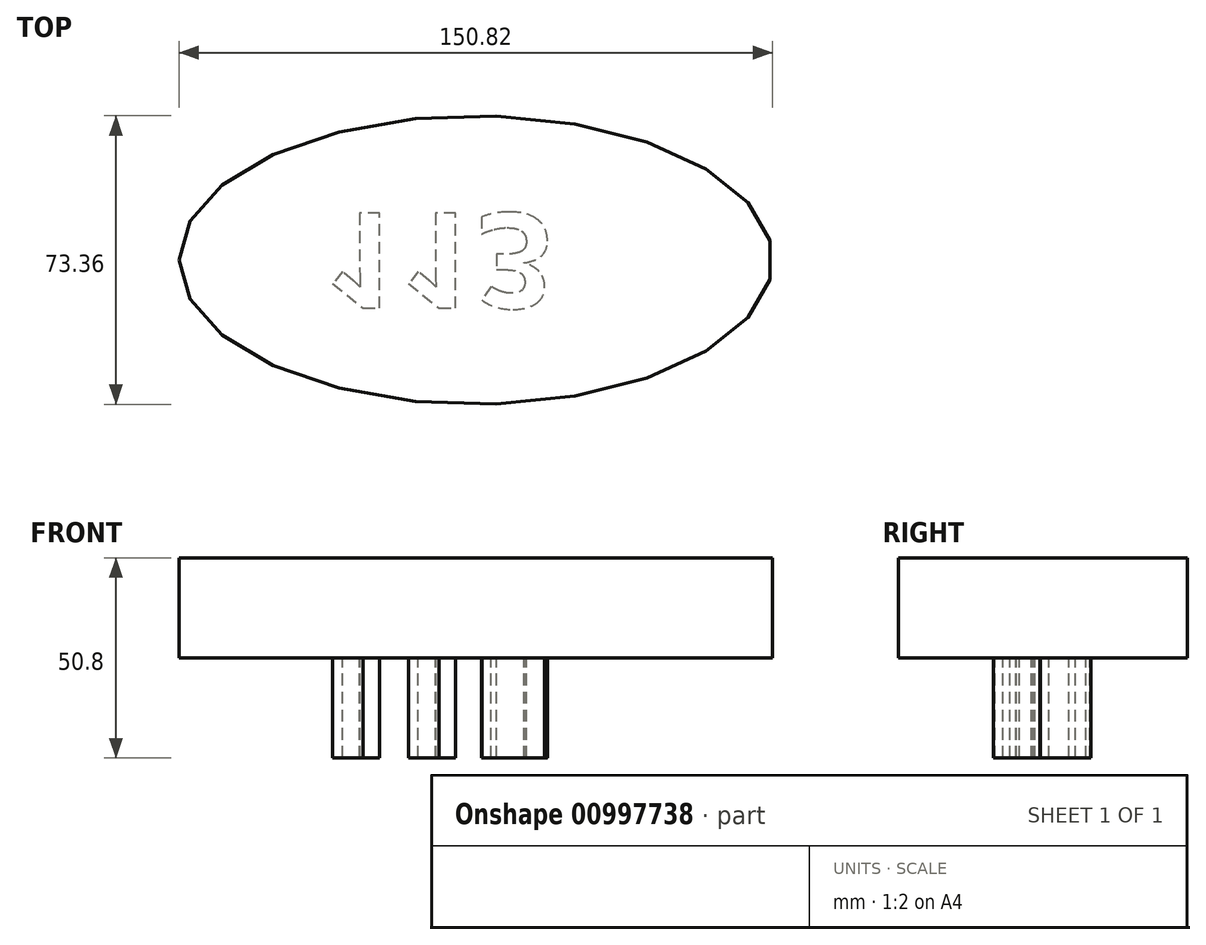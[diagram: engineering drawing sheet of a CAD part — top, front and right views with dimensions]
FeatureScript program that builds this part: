
annotation { "Feature Type Name" : "Feature", "Feature Type Description" : "" }
export const myFeature = defineFeature(function(context is Context, id is Id, definition is map)
    precondition{}
    {
        {
            var Q0;
            Q0=qCreatedBy(makeId("Top.planeOp"),FACE);
            var sketch = newSketch(context, id + "F0", { "sketchPlane" : qUnion([Q0])});
            skEllipse(sketch, "E0", {"center": v(0, 0) * mm, "majorRadius": 75.41 * mm, "minorRadius": 36.68 * mm, "majorAxis": v(-1, 0)});
            skSolve(sketch);
        }
        {
            var Q0;
            Q0 = qSketchRegion(id + "F0", true);
            extrude(context, id + "F1", {"entities" : qUnion([Q0]), "depth" : 25.4 * mm, "offsetDistance" : 25.4 * mm});
        }
        {
            var Q0;
            Q0=makeQuery(id+"F1.opExtrude","CAP_FACE",FACE,{"disambiguationData":[OSD([sQuery(id+"F0.wireOp",EDGE,"E0")])],"isStart":true});
            var sketch = newSketch(context, id + "F2", { "sketchPlane" : qUnion([Q0])});
            skText(sketch, "E1", { "text": "113\n", "fontName": "OpenSans-Bold.ttf"});
            const initialGuessF2  = {"E1": [-0.03835, -0.01191, 1, 0, 0.02433]};
            skSetInitialGuess(sketch, initialGuessF2);
            skSolve(sketch);
        }
        {
            var Q0;
            Q0 = qSketchRegion(id + "F2", true);
            extrude(context, id + "F3", {"entities" : qUnion([Q0]), "operationType" : NewBodyOperationType.ADD, "depth" : 25.4 * mm, "offsetDistance" : 25.4 * mm});
        }
    });
